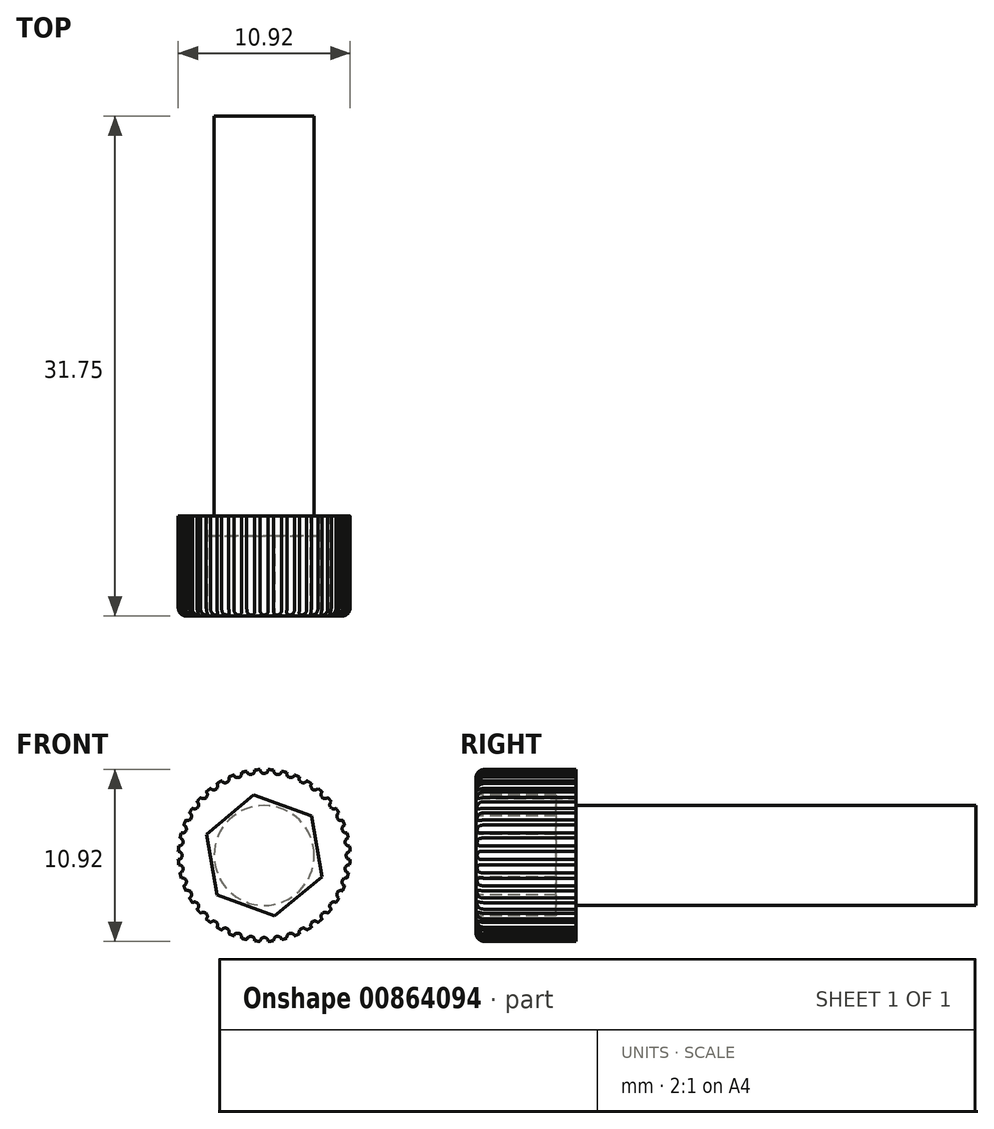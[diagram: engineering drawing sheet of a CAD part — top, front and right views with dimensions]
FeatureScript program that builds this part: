
annotation { "Feature Type Name" : "Feature", "Feature Type Description" : "" }
export const myFeature = defineFeature(function(context is Context, id is Id, definition is map)
    precondition{}
    {
        {
            var Q0;
            Q0=qCreatedBy(makeId("Front.planeOp"),FACE);
            var sketch = newSketch(context, id + "F0", { "sketchPlane" : qUnion([Q0])});
            skCircle(sketch, "E0", {"center": v(0, 0) * mm, "radius": 3.18 * mm});
            skCircle(sketch, "E1", {"center": v(0, 0) * mm, "radius": 5.46 * mm});
            skSolve(sketch);
        }
        {
            var Q0;
            Q0=makeQuery(id+"F0.imprint","IMPRINT",FACE,{"disambiguationData":[TD([[makeQuery(id+"F0.imprint","IMPRINT",EDGE,{"derivedFrom":sQuery(id+"F0.wireOp",EDGE,"E0")}),1.0]])]});
            extrude(context, id + "F1", {"entities" : qUnion([Q0]), "oppositeDirection" : true, "depth" : 25.4 * mm, "offsetDistance" : 25.4 * mm});
        }
        {
            var Q0;
            Q0=makeQuery(id+"F0.imprint","IMPRINT",FACE,{"disambiguationData":[TD([[makeQuery(id+"F0.imprint","IMPRINT",EDGE,{"derivedFrom":sQuery(id+"F0.wireOp",EDGE,"E0")}),-1.0]])]});
            var Q1;
            Q1=makeQuery(id+"F0.imprint","IMPRINT",FACE,{"disambiguationData":[TD([[makeQuery(id+"F0.imprint","IMPRINT",EDGE,{"derivedFrom":sQuery(id+"F0.wireOp",EDGE,"E0")}),1.0]])]});
            extrude(context, id + "F2", {"entities" : qUnion([Q0, Q1]), "operationType" : NewBodyOperationType.ADD, "depth" : 6.35 * mm, "offsetDistance" : 25.4 * mm});
        }
        {
            var Q0;
            Q0=makeQuery(id+"F2.opExtrude","CAP_FACE",FACE,{"disambiguationData":[OSD([sQuery(id+"F0.wireOp",EDGE,"E1")])],"isStart":false});
            var sketch = newSketch(context, id + "F3", { "sketchPlane" : qUnion([Q0])});
            skCircle(sketch, "E2.cCircle", {"center": v(0, 0) * mm, "radius": 3.38 * mm, "construction": true});
            skLineSegment(sketch, "E2.0", {"start": v(-3.66, 1.35) * mm, "end": v(-0.67, 3.85) * mm});
            skLineSegment(sketch, "E2.1", {"start": v(-0.67, 3.85) * mm, "end": v(3, 2.5) * mm});
            skLineSegment(sketch, "E2.2", {"start": v(3, 2.5) * mm, "end": v(3.66, -1.35) * mm});
            skLineSegment(sketch, "E2.3", {"start": v(3.66, -1.35) * mm, "end": v(0.67, -3.85) * mm});
            skLineSegment(sketch, "E2.4", {"start": v(0.67, -3.85) * mm, "end": v(-3, -2.5) * mm});
            skLineSegment(sketch, "E2.5", {"start": v(-3, -2.5) * mm, "end": v(-3.66, 1.35) * mm});
            skPoint(sketch, "E2.0.midPoint", {"position": v(-2.17, 2.6) * mm});
            skSolve(sketch);
        }
        {
            var Q0;
            Q0=makeQuery(id+"F3.imprint","IMPRINT",FACE,{"disambiguationData":[TD([[makeQuery(id+"F3.imprint","IMPRINT",EDGE,{"derivedFrom":sQuery(id+"F3.wireOp",EDGE,"E2.0")}),-1.0]])]});
            extrude(context, id + "F4", {"entities" : qUnion([Q0]), "operationType" : NewBodyOperationType.REMOVE, "oppositeDirection" : true, "depth" : 5.08 * mm, "offsetDistance" : 25.4 * mm});
        }
        {
            var Q0;
            Q0=makeQuery(id+"F2.opExtrude","CAP_EDGE",EDGE,{"disambiguationData":[OSD([sQuery(id+"F0.wireOp",EDGE,"E1")])],"isStart":false});
            fillet(context, id + "F5", {"entities" : qUnion([Q0]), "radius" : 0.5 * mm, "tangentPropagation" : true, "allowEdgeOverflow" : false});
        }
        {
            var Q0;
            Q0=qCreatedBy(makeId("Front.planeOp"),FACE);
            var sketch = newSketch(context, id + "F6", { "sketchPlane" : qUnion([Q0])});
            skCircle(sketch, "E3", {"center": v(0, 5.46) * mm, "radius": 0.25 * mm});
            skCircle(sketch, "E4.1.0", {"center": v(-0.85, 5.4) * mm, "radius": 0.25 * mm});
            skCircle(sketch, "E4.2.0", {"center": v(-1.69, 5.2) * mm, "radius": 0.25 * mm});
            skCircle(sketch, "E4.3.0", {"center": v(-2.48, 4.87) * mm, "radius": 0.25 * mm});
            skCircle(sketch, "E4.4.0", {"center": v(-3.2, 4.42) * mm, "radius": 0.25 * mm});
            skCircle(sketch, "E4.5.0", {"center": v(-3.86, 3.86) * mm, "radius": 0.25 * mm});
            skCircle(sketch, "E4.6.0", {"center": v(-4.42, 3.2) * mm, "radius": 0.25 * mm});
            skCircle(sketch, "E4.7.0", {"center": v(-4.87, 2.48) * mm, "radius": 0.25 * mm});
            skCircle(sketch, "E4.8.0", {"center": v(-5.2, 1.69) * mm, "radius": 0.25 * mm});
            skCircle(sketch, "E4.9.0", {"center": v(-5.4, 0.85) * mm, "radius": 0.25 * mm});
            skCircle(sketch, "E4.10.0", {"center": v(-5.46, 0) * mm, "radius": 0.25 * mm});
            skCircle(sketch, "E4.11.0", {"center": v(-5.4, -0.85) * mm, "radius": 0.25 * mm});
            skCircle(sketch, "E4.12.0", {"center": v(-5.2, -1.69) * mm, "radius": 0.25 * mm});
            skCircle(sketch, "E4.13.0", {"center": v(-4.87, -2.48) * mm, "radius": 0.25 * mm});
            skCircle(sketch, "E4.14.0", {"center": v(-4.42, -3.2) * mm, "radius": 0.25 * mm});
            skCircle(sketch, "E4.15.0", {"center": v(-3.86, -3.86) * mm, "radius": 0.25 * mm});
            skCircle(sketch, "E4.16.0", {"center": v(-3.2, -4.42) * mm, "radius": 0.25 * mm});
            skCircle(sketch, "E4.17.0", {"center": v(-2.48, -4.87) * mm, "radius": 0.25 * mm});
            skCircle(sketch, "E4.18.0", {"center": v(-1.69, -5.2) * mm, "radius": 0.25 * mm});
            skCircle(sketch, "E4.19.0", {"center": v(-0.85, -5.4) * mm, "radius": 0.25 * mm});
            skCircle(sketch, "E4.20.0", {"center": v(0, -5.46) * mm, "radius": 0.25 * mm});
            skCircle(sketch, "E4.21.0", {"center": v(0.85, -5.4) * mm, "radius": 0.25 * mm});
            skCircle(sketch, "E4.22.0", {"center": v(1.69, -5.2) * mm, "radius": 0.25 * mm});
            skCircle(sketch, "E4.23.0", {"center": v(2.48, -4.87) * mm, "radius": 0.25 * mm});
            skCircle(sketch, "E4.24.0", {"center": v(3.2, -4.42) * mm, "radius": 0.25 * mm});
            skCircle(sketch, "E4.25.0", {"center": v(3.86, -3.86) * mm, "radius": 0.25 * mm});
            skCircle(sketch, "E4.26.0", {"center": v(4.42, -3.2) * mm, "radius": 0.25 * mm});
            skCircle(sketch, "E4.27.0", {"center": v(4.87, -2.48) * mm, "radius": 0.25 * mm});
            skCircle(sketch, "E4.28.0", {"center": v(5.2, -1.69) * mm, "radius": 0.25 * mm});
            skCircle(sketch, "E4.29.0", {"center": v(5.4, -0.85) * mm, "radius": 0.25 * mm});
            skCircle(sketch, "E4.30.0", {"center": v(5.46, 0) * mm, "radius": 0.25 * mm});
            skCircle(sketch, "E4.31.0", {"center": v(5.4, 0.85) * mm, "radius": 0.25 * mm});
            skCircle(sketch, "E4.32.0", {"center": v(5.2, 1.69) * mm, "radius": 0.25 * mm});
            skCircle(sketch, "E4.33.0", {"center": v(4.87, 2.48) * mm, "radius": 0.25 * mm});
            skCircle(sketch, "E4.34.0", {"center": v(4.42, 3.2) * mm, "radius": 0.25 * mm});
            skCircle(sketch, "E4.35.0", {"center": v(3.86, 3.86) * mm, "radius": 0.25 * mm});
            skCircle(sketch, "E4.36.0", {"center": v(3.2, 4.42) * mm, "radius": 0.25 * mm});
            skCircle(sketch, "E4.37.0", {"center": v(2.48, 4.87) * mm, "radius": 0.25 * mm});
            skCircle(sketch, "E4.38.0", {"center": v(1.69, 5.2) * mm, "radius": 0.25 * mm});
            skCircle(sketch, "E4.39.0", {"center": v(0.85, 5.4) * mm, "radius": 0.25 * mm});
            skPoint(sketch, "E4.center", {"position": v(0, 0) * mm});
            skSolve(sketch);
        }
        {
            var Q0;
            Q0 = qSketchRegion(id + "F6", true);
            extrude(context, id + "F7", {"entities" : qUnion([Q0]), "operationType" : NewBodyOperationType.REMOVE, "endBound" : BoundingType.THROUGH_ALL, "depth" : 25.4 * mm, "offsetDistance" : 25.4 * mm});
        }
    });
